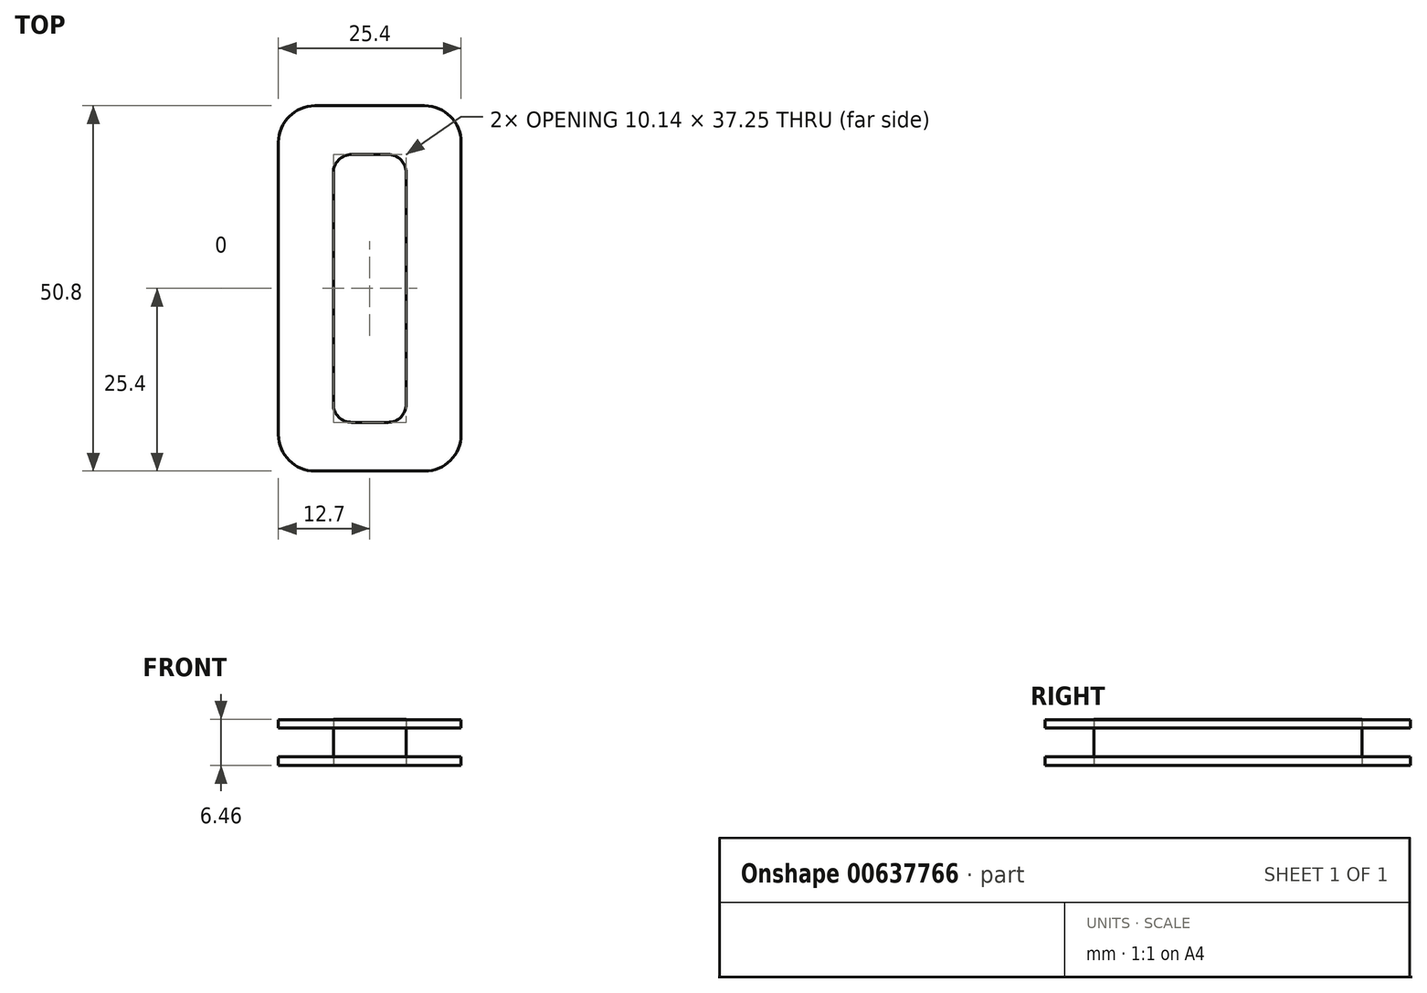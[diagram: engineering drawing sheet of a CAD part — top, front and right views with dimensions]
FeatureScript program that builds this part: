
annotation { "Feature Type Name" : "Feature", "Feature Type Description" : "" }
export const myFeature = defineFeature(function(context is Context, id is Id, definition is map)
    precondition{}
    {
        {
            var Q0;
            Q0=qCreatedBy(makeId("Top.planeOp"),FACE);
            var sketch = newSketch(context, id + "F0", { "sketchPlane" : qUnion([Q0])});
            skLineSegment(sketch, "E0.bottom", {"start": v(7.62, 25.4) * mm, "end": v(-7.62, 25.4) * mm});
            skLineSegment(sketch, "E0.top", {"start": v(7.62, -25.4) * mm, "end": v(-7.62, -25.4) * mm});
            skLineSegment(sketch, "E0.left", {"start": v(12.7, 20.32) * mm, "end": v(12.7, -20.32) * mm});
            skLineSegment(sketch, "E0.right", {"start": v(-12.7, 20.32) * mm, "end": v(-12.7, -20.32) * mm});
            skPoint(sketch, "E0.middle", {"position": v(0, 0) * mm});
            skLineSegment(sketch, "E1.bottom", {"start": v(2.53, 18.63) * mm, "end": v(-2.53, 18.63) * mm});
            skLineSegment(sketch, "E1.top", {"start": v(2.53, -18.63) * mm, "end": v(-2.53, -18.63) * mm});
            skLineSegment(sketch, "E1.left", {"start": v(5.07, 16.09) * mm, "end": v(5.07, -16.09) * mm});
            skLineSegment(sketch, "E1.right", {"start": v(-5.07, 16.09) * mm, "end": v(-5.07, -16.09) * mm});
            skPoint(sketch, "E2.visualSharp", {"position": v(-5.07, 18.63) * mm});
            skArc(sketch, "E2.filletArc", {"start": v(-2.53, 18.63) * mm, "mid": v(-4.32, 17.88) * mm, "end": v(-5.07, 16.09) * mm});
            skPoint(sketch, "E3.visualSharp", {"position": v(5.07, 18.63) * mm});
            skArc(sketch, "E3.filletArc", {"start": v(5.07, 16.09) * mm, "mid": v(4.32, 17.88) * mm, "end": v(2.53, 18.63) * mm});
            skPoint(sketch, "E4.visualSharp", {"position": v(5.07, -18.63) * mm});
            skArc(sketch, "E4.filletArc", {"start": v(2.53, -18.63) * mm, "mid": v(4.32, -17.88) * mm, "end": v(5.07, -16.09) * mm});
            skPoint(sketch, "E5.visualSharp", {"position": v(-5.07, -18.63) * mm});
            skArc(sketch, "E5.filletArc", {"start": v(-5.07, -16.09) * mm, "mid": v(-4.32, -17.88) * mm, "end": v(-2.53, -18.63) * mm});
            skPoint(sketch, "E6.visualSharp", {"position": v(-12.7, 25.4) * mm});
            skArc(sketch, "E6.filletArc", {"start": v(-7.62, 25.4) * mm, "mid": v(-11.21, 23.91) * mm, "end": v(-12.7, 20.32) * mm});
            skPoint(sketch, "E7.visualSharp", {"position": v(12.7, 25.4) * mm});
            skArc(sketch, "E7.filletArc", {"start": v(12.7, 20.32) * mm, "mid": v(11.21, 23.91) * mm, "end": v(7.62, 25.4) * mm});
            skPoint(sketch, "E8.visualSharp", {"position": v(12.7, -25.4) * mm});
            skArc(sketch, "E8.filletArc", {"start": v(7.62, -25.4) * mm, "mid": v(11.21, -23.91) * mm, "end": v(12.7, -20.32) * mm});
            skPoint(sketch, "E9.visualSharp", {"position": v(-12.7, -25.4) * mm});
            skArc(sketch, "E9.filletArc", {"start": v(-12.7, -20.32) * mm, "mid": v(-11.21, -23.91) * mm, "end": v(-7.62, -25.4) * mm});
            skSolve(sketch);
        }
        {
            var Q0;
            Q0=makeQuery(id+"F0.imprint","IMPRINT",FACE,{"disambiguationData":[TD([[makeQuery(id+"F0.imprint","IMPRINT",EDGE,{"derivedFrom":sQuery(id+"F0.wireOp",EDGE,"E0.bottom")}),1.0]])]});
            extrude(context, id + "F1", {"entities" : qUnion([Q0]), "endBound" : BoundingType.SYMMETRIC, "depth" : 6.35 * mm, "offsetDistance" : 25.4 * mm, "hasSecondDirectionOffset" : true, "secondDirectionOffsetDistance" : 25.4 * mm});
        }
        {
            var Q0;
            Q0=makeQuery(id+"F1.opExtrude","SWEPT_FACE",FACE,{"disambiguationData":[OSD([sQuery(id+"F0.wireOp",EDGE,"E0.right")])]});
            var sketch = newSketch(context, id + "F2", { "sketchPlane" : qUnion([Q0])});
            skLineSegment(sketch, "E10.bottom", {"start": v(27.6, 2) * mm, "end": v(-27.6, 2) * mm});
            skLineSegment(sketch, "E10.top", {"start": v(27.6, -2) * mm, "end": v(-27.6, -2) * mm});
            skLineSegment(sketch, "E10.left", {"start": v(27.6, 2) * mm, "end": v(27.6, -2) * mm});
            skLineSegment(sketch, "E10.right", {"start": v(-27.6, 2) * mm, "end": v(-27.6, -2) * mm});
            skPoint(sketch, "E10.middle", {"position": v(0, 0) * mm});
            skSolve(sketch);
        }
        {
            var Q0;
            Q0 = qSketchRegion(id + "F2", true);
            extrude(context, id + "F3", {"entities" : qUnion([Q0]), "operationType" : NewBodyOperationType.REMOVE, "oppositeDirection" : true, "depth" : 25.4 * mm, "offsetDistance" : 25.4 * mm});
        }
        {
            var Q0;
            Q0=makeQuery(id+"F0.imprint","IMPRINT",FACE,{"disambiguationData":[TD([[makeQuery(id+"F0.imprint","IMPRINT",EDGE,{"derivedFrom":sQuery(id+"F0.wireOp",EDGE,"E1.bottom")}),1.0]])]});
            extrude(context, id + "F4", {"entities" : qUnion([Q0]), "endBound" : BoundingType.SYMMETRIC, "depth" : 6.45 * mm, "offsetDistance" : 25.4 * mm});
        }
    });
